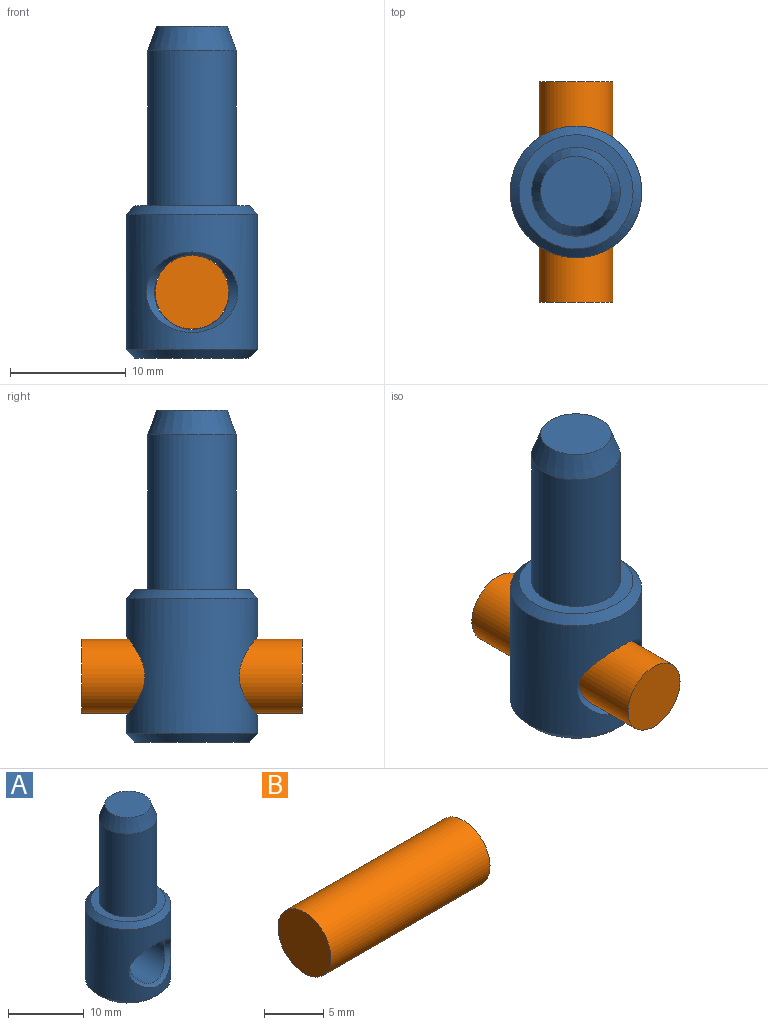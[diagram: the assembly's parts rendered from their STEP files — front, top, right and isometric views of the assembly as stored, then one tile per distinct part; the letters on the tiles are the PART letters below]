
ASSEMBLY  parts=2 mates=1
PART A: 11 faces, bbox 11.4x11.4x28.6 mm
  f0: plane 6.1x6.1mm, normal (0,0,1), area 29.2mm2, adj f6
  f1: cylinder r=3.82mm len=13.37mm, axis (0,0,1), area 321.1mm2, adj f2,f6
  f2: plane 9.85x9.85mm, normal (0,0,1), area 30.3mm2, adj f1,f8
  f3: cylinder r=5.68mm len=11.65mm, axis (0,0,1), area 322.4mm2, adj f7,f8,f9,f10
  f4: plane 9.85x9.85mm, normal (0,0,-1), area 76.2mm2, adj f7
  f5: cylinder r=3.23mm len=9.98mm, axis (0,-1,0), area 202.2mm2, adj f9,f10
  f6: cone r=3.05mm half-angle=20deg, axis (0,0,-1), area 48.9mm2, adj f0,f1
  f7: cone r=5.68mm half-angle=45deg, axis (0,0,1), area 35.3mm2, adj f3,f4
  f8: cone r=4.92mm half-angle=45deg, axis (0,0,-1), area 35.3mm2, adj f2,f3
  f9: bspline ~7.91x6.95mm, area 18.4mm2, adj f3,f5
  f10: bspline ~7.91x6.95mm, area 18.4mm2, adj f3,f5
PART B: 3 faces, bbox 19.1x6.4x6.4 mm
  f0: cylinder r=3.17mm len=19.05mm, axis (-1,0,0), area 380mm2, adj f1,f2
  f1: plane 6.35x6.35mm, normal (1,0,0), area 31.7mm2, adj f0
  f2: plane 6.35x6.35mm, normal (-1,0,0), area 31.7mm2, adj f0
PLACE A at identity fixed
PLACE B rot(axis=(-0.58,-0.58,0.58),120deg) t=(0,0,-8.65)mm
MATE revolute B.f0 <-> A.f5  axis (0,-1,0) through (0,0,-8.65)mm
